# Revit family: Grohe_PlumbingFixture_CostaL_WallSinkMixer_31191001a
name_source: partatom
category: Plumbing Fixtures
revit_build: Autodesk Revit 2018 (Build: 20190510_1515(x64)
units: mm (PartAtom-declared; Revit-internal decimal feet)

## family parameters
Cut with Voids When Loaded = No
Host = Face
OmniClass Number = 23.65.00.00
OmniClass Title = Supply and Distribution of Liquids and Gases
Part Type = Normal
Room Calculation Point = No
Round Connector Dimension = Use Diameter
Shared = No

## types (1)
- 31191001
    ADACompliant = No
    Assembly Code = D2020300
    BIMObjectName = Grohe_PlumbingFixture_CostaL_WallSinkMixer_31191001
    CWFU = 4.5
    ClassificationName = Uniclass 2015
    ClassificationValue = Pr_40_20_87_98
    ColdWaterConnectionDiameter = 10 mm  [stored 0.0328084 ft]
    Color = Chrome
    Default Elevation = 0 mm  [stored 0 ft]
    Description = A perfect fusion of German engineering and beautiful yet timeless design! The wall-mounted GROHE Costa L sink mixer makes a serious style statement in any contemporary bathroom. Packed with GROHE technology, the impressive tap is made from the finest materials to ensure it lasts a lifetime and is a pleasure to operate. The tall swivel spout with mousseur is super convenient and can be turned with the lightest touch and the gleaming GROHE StarLight chrome coating is scratch-resistant and very easy to clean – a quick wipe and it looks shiny and new. GROHE Costa – a quick kitchen upgrade that balances style with everyday performance you can trust!
    DocumentationCertificates = https://www.bimstore.co
    DocumentationInstallationGuide = https://www.bimstore.co
    DocumentationLiterature = https://www.bimstore.co
    DocumentationMaintenance = https://www.bimstore.co
    DocumentationTechnical = https://www.bimstore.co
    DurationUnit = Years
    Ecojoy = No
    ExpectedLife = 0
    Features = A perfect fusion of German engineering and beautiful yet timeless design! The wall-mounted GROHE Costa L sink mixer makes a serious style statement in any contemporary bathroom. Packed with GROHE technology, the impressive tap is made from the finest materials to ensure it lasts a lifetime and is a pleasure to operate. The tall swivel spout with mousseur is super convenient and can be turned with the lightest touch and the gleaming GROHE StarLight chrome coating is scratch-resistant and very easy to clean – a quick wipe and it looks shiny and new. GROHE Costa – a quick kitchen upgrade that balances style with everyday performance you can trust!
    HWFU = 4.5
    HotWaterConnectionDiameter = 10 mm  [stored 0.0328084 ft]
    IfcExportAs = IfcPipeFitting
    IfcExportType = IfcPipeFittingType
    Keynote = N13
    LowEmittingMaterial = No
    Manufacturer = Grohe
    ManufacturerName = Grohe
    MasterformatNumber = 01 52 19
    MasterformatTitle = Sanitary Facilities
    Model = Costa L - Wall sink mixer 1/2″
    ModelNumber = 31191001
    ModelReference = Costa L - Wall sink mixer 1/2″
    NBSDescription = Water supply fittings for wash basins and troughs
    NBSObjectName = Grohe - Water supply fittings for wash basins and troughs
    NBSReference = 45-35-70/371
    NominalDepth = 0 mm  [stored 0 ft]
    NominalHeight = 0 mm  [stored 0 ft]
    NominalLength = 0 mm  [stored 0 ft]
    PrimaryMaterial = Steel, Chrome Plated
    ProductDocumentationLink = https://www.grohe-middleeast.com
    ProductPageURL = https://www.grohe-middleeast.com
    ProductionYear = 2020
    Type Comments = 31191001
    TypeName = Costa L - Wall sink mixer 1/2″
    URL = https://www.grohe.co.uk
    WarrantyDurationLabor = 0
    WarrantyDurationParts = 0
    WarrantyDurationUnit = Years
    _BSBibleVersion = 16
    _BimSpecGuid = 0
    _CurrentRevision = 1
    _DistributedBy = www.bimstore.co
    _ObjectUserGuide = https://www.bimstore.co

note: [stored X ft] marks values corroborated as IEEE doubles in the binary element streams (Revit-internal decimal feet)

## geometry (parser evidence)
native form markers: Sweep x1
no freeform markers — native parametric forms only
